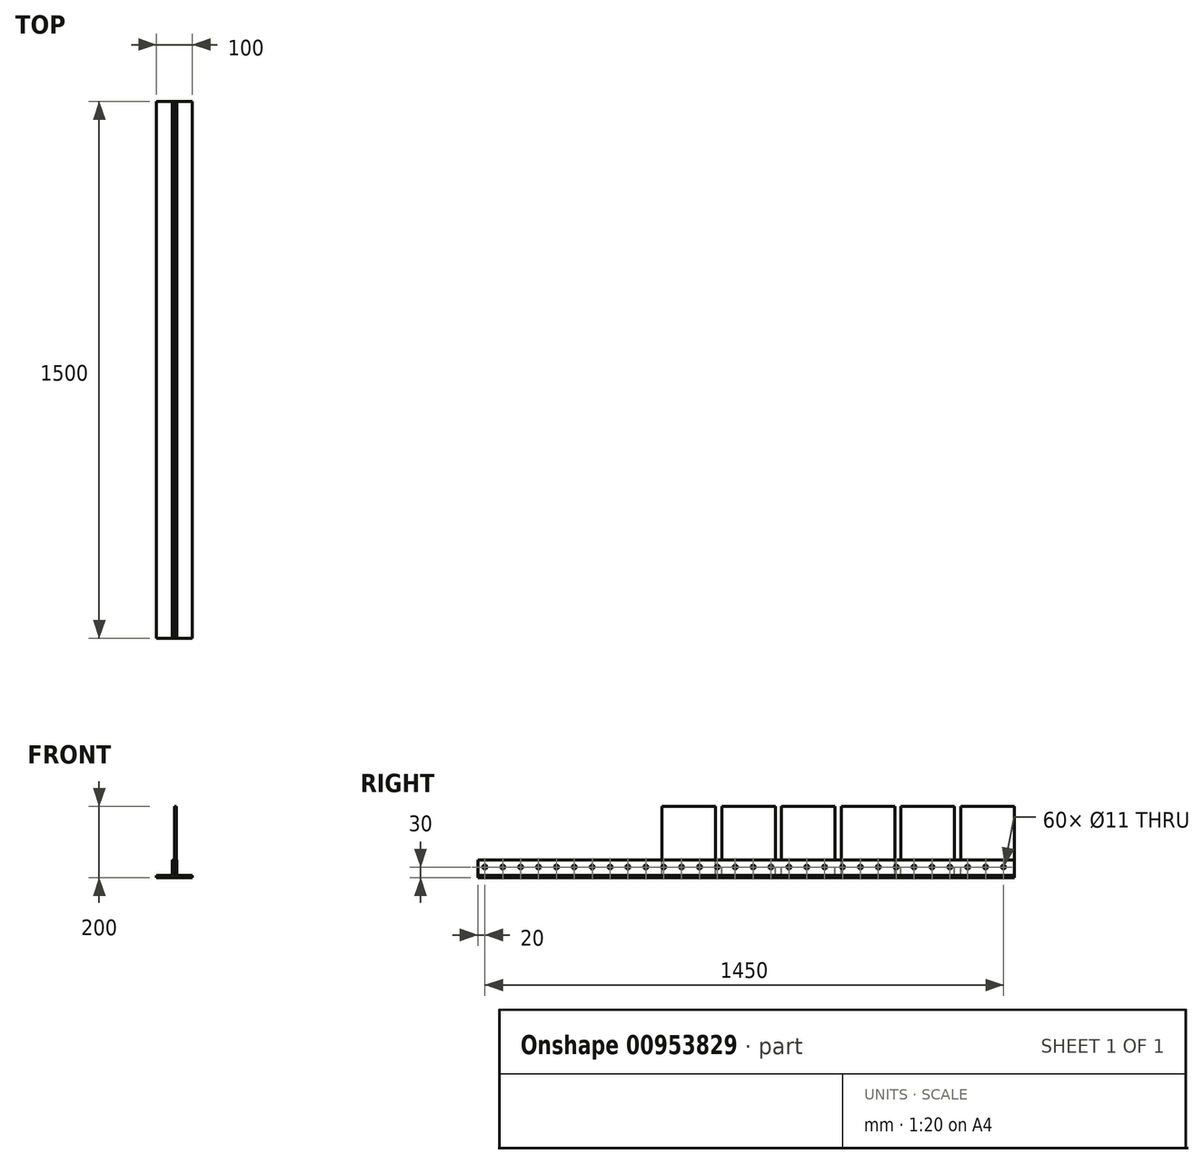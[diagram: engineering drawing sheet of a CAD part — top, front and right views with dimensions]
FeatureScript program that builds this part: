
annotation { "Feature Type Name" : "Feature", "Feature Type Description" : "" }
export const myFeature = defineFeature(function(context is Context, id is Id, definition is map)
    precondition{}
    {
        {
            var Q0;
            Q0=qCreatedBy(makeId("Front.planeOp"),FACE);
            var sketch = newSketch(context, id + "F0", { "sketchPlane" : qUnion([Q0])});
            skLineSegment(sketch, "E0", {"start": v(0, 0) * mm, "end": v(50, 0) * mm});
            skLineSegment(sketch, "E1", {"start": v(50, 0) * mm, "end": v(50, 6) * mm});
            skLineSegment(sketch, "E2", {"start": v(50, 6) * mm, "end": v(6, 6) * mm});
            skLineSegment(sketch, "E3", {"start": v(6, 6) * mm, "end": v(6, 50) * mm});
            skLineSegment(sketch, "E4", {"start": v(6, 50) * mm, "end": v(0, 50) * mm});
            skLineSegment(sketch, "E5", {"start": v(0, 50) * mm, "end": v(0, 0) * mm});
            skSolve(sketch);
        }
        {
            var Q0;
            Q0 = qSketchRegion(id + "F0", true);
            extrude(context, id + "F1", {"entities" : qUnion([Q0]), "depth" : 1500 * mm, "offsetDistance" : 25 * mm});
        }
        {
            var Q0;
            Q0=qCreatedBy(makeId("Right.planeOp"),FACE);
            var sketch = newSketch(context, id + "F2", { "sketchPlane" : qUnion([Q0])});
            skLineSegment(sketch, "E6", {"start": v(0, 0) * mm, "end": v(0, 30) * mm});
            skLineSegment(sketch, "E7", {"start": v(0, 30) * mm, "end": v(-30, 30) * mm});
            skCircle(sketch, "E8", {"center": v(-30, 30) * mm, "radius": 5.5 * mm});
            skCircle(sketch, "E9.1.0.0", {"center": v(-80, 30) * mm, "radius": 5.5 * mm});
            skCircle(sketch, "E9.2.0.0", {"center": v(-130, 30) * mm, "radius": 5.5 * mm});
            skCircle(sketch, "E9.3.0.0", {"center": v(-180, 30) * mm, "radius": 5.5 * mm});
            skCircle(sketch, "E9.4.0.0", {"center": v(-230, 30) * mm, "radius": 5.5 * mm});
            skCircle(sketch, "E9.5.0.0", {"center": v(-280, 30) * mm, "radius": 5.5 * mm});
            skCircle(sketch, "E9.6.0.0", {"center": v(-330, 30) * mm, "radius": 5.5 * mm});
            skCircle(sketch, "E9.7.0.0", {"center": v(-380, 30) * mm, "radius": 5.5 * mm});
            skCircle(sketch, "E9.8.0.0", {"center": v(-430, 30) * mm, "radius": 5.5 * mm});
            skCircle(sketch, "E9.9.0.0", {"center": v(-480, 30) * mm, "radius": 5.5 * mm});
            skCircle(sketch, "E9.10.0.0", {"center": v(-530, 30) * mm, "radius": 5.5 * mm});
            skCircle(sketch, "E9.11.0.0", {"center": v(-580, 30) * mm, "radius": 5.5 * mm});
            skCircle(sketch, "E9.12.0.0", {"center": v(-630, 30) * mm, "radius": 5.5 * mm});
            skCircle(sketch, "E9.13.0.0", {"center": v(-680, 30) * mm, "radius": 5.5 * mm});
            skCircle(sketch, "E9.14.0.0", {"center": v(-730, 30) * mm, "radius": 5.5 * mm});
            skCircle(sketch, "E9.15.0.0", {"center": v(-780, 30) * mm, "radius": 5.5 * mm});
            skCircle(sketch, "E9.16.0.0", {"center": v(-830, 30) * mm, "radius": 5.5 * mm});
            skCircle(sketch, "E9.17.0.0", {"center": v(-880, 30) * mm, "radius": 5.5 * mm});
            skCircle(sketch, "E9.18.0.0", {"center": v(-930, 30) * mm, "radius": 5.5 * mm});
            skCircle(sketch, "E9.19.0.0", {"center": v(-980, 30) * mm, "radius": 5.5 * mm});
            skCircle(sketch, "E9.20.0.0", {"center": v(-1030, 30) * mm, "radius": 5.5 * mm});
            skCircle(sketch, "E9.21.0.0", {"center": v(-1080, 30) * mm, "radius": 5.5 * mm});
            skCircle(sketch, "E9.22.0.0", {"center": v(-1130, 30) * mm, "radius": 5.5 * mm});
            skCircle(sketch, "E9.23.0.0", {"center": v(-1180, 30) * mm, "radius": 5.5 * mm});
            skCircle(sketch, "E9.24.0.0", {"center": v(-1230, 30) * mm, "radius": 5.5 * mm});
            skCircle(sketch, "E9.25.0.0", {"center": v(-1280, 30) * mm, "radius": 5.5 * mm});
            skCircle(sketch, "E9.26.0.0", {"center": v(-1330, 30) * mm, "radius": 5.5 * mm});
            skCircle(sketch, "E9.27.0.0", {"center": v(-1380, 30) * mm, "radius": 5.5 * mm});
            skCircle(sketch, "E9.28.0.0", {"center": v(-1430, 30) * mm, "radius": 5.5 * mm});
            skCircle(sketch, "E9.29.0.0", {"center": v(-1480, 30) * mm, "radius": 5.5 * mm});
            skLineSegment(sketch, "E9.direction1", {"start": v(-30, 30) * mm, "end": v(-80, 30) * mm, "construction": true});
            skSolve(sketch);
        }
        {
            var Q0;
            Q0=sQuery(id+"F2.wireOp",VERTEX,"E7.end");
            var Q1;
            Q1=sQuery(id+"F2.wireOp",VERTEX,"E9.direction1.end");
            var Q2;
            Q2=sQuery(id+"F2.wireOp",VERTEX,"E9.2.0.0.center");
            var Q3;
            Q3=sQuery(id+"F2.wireOp",VERTEX,"E9.3.0.0.center");
            var Q4;
            Q4=sQuery(id+"F2.wireOp",VERTEX,"E9.4.0.0.center");
            var Q5;
            Q5=sQuery(id+"F2.wireOp",VERTEX,"E9.5.0.0.center");
            var Q6;
            Q6=sQuery(id+"F2.wireOp",VERTEX,"E9.6.0.0.center");
            var Q7;
            Q7=sQuery(id+"F2.wireOp",VERTEX,"E9.7.0.0.center");
            var Q8;
            Q8=sQuery(id+"F2.wireOp",VERTEX,"E9.8.0.0.center");
            var Q9;
            Q9=sQuery(id+"F2.wireOp",VERTEX,"E9.9.0.0.center");
            var Q10;
            Q10=sQuery(id+"F2.wireOp",VERTEX,"E9.10.0.0.center");
            var Q11;
            Q11=sQuery(id+"F2.wireOp",VERTEX,"E9.11.0.0.center");
            var Q12;
            Q12=sQuery(id+"F2.wireOp",VERTEX,"E9.12.0.0.center");
            var Q13;
            Q13=sQuery(id+"F2.wireOp",VERTEX,"E9.13.0.0.center");
            var Q14;
            Q14=sQuery(id+"F2.wireOp",VERTEX,"E9.14.0.0.center");
            var Q15;
            Q15=sQuery(id+"F2.wireOp",VERTEX,"E9.15.0.0.center");
            var Q16;
            Q16=sQuery(id+"F2.wireOp",VERTEX,"E9.16.0.0.center");
            var Q17;
            Q17=sQuery(id+"F2.wireOp",VERTEX,"E9.17.0.0.center");
            var Q18;
            Q18=sQuery(id+"F2.wireOp",VERTEX,"E9.18.0.0.center");
            var Q19;
            Q19=sQuery(id+"F2.wireOp",VERTEX,"E9.19.0.0.center");
            var Q20;
            Q20=sQuery(id+"F2.wireOp",VERTEX,"E9.20.0.0.center");
            var Q21;
            Q21=sQuery(id+"F2.wireOp",VERTEX,"E9.21.0.0.center");
            var Q22;
            Q22=sQuery(id+"F2.wireOp",VERTEX,"E9.22.0.0.center");
            var Q23;
            Q23=sQuery(id+"F2.wireOp",VERTEX,"E9.23.0.0.center");
            var Q24;
            Q24=sQuery(id+"F2.wireOp",VERTEX,"E9.24.0.0.center");
            var Q25;
            Q25=sQuery(id+"F2.wireOp",VERTEX,"E9.25.0.0.center");
            var Q26;
            Q26=sQuery(id+"F2.wireOp",VERTEX,"E9.26.0.0.center");
            var Q27;
            Q27=sQuery(id+"F2.wireOp",VERTEX,"E9.27.0.0.center");
            var Q28;
            Q28=sQuery(id+"F2.wireOp",VERTEX,"E9.28.0.0.center");
            var Q29;
            Q29=sQuery(id+"F2.wireOp",VERTEX,"E9.29.0.0.center");
            var Q30;
            Q30=makeQuery(id+"F1.opExtrude","SWEPT_BODY",BODY,{"disambiguationData":[OSD([sQuery(id+"F0.wireOp",EDGE,"E0"),sQuery(id+"F0.wireOp",EDGE,"E1"),sQuery(id+"F0.wireOp",EDGE,"E2"),sQuery(id+"F0.wireOp",EDGE,"E3"),sQuery(id+"F0.wireOp",EDGE,"E4"),sQuery(id+"F0.wireOp",EDGE,"E5")])]});
            hole(context, id + "F3", {"style" : HoleStyle.SIMPLE, "endStyle" : HoleEndStyle.THROUGH, "oppositeDirection" : true, "holeDiameter" : 11 * mm, "majorDiameter" : 5 * mm, "isTappedThrough" : true, "tappedDepth" : 14.75 * mm, "tapClearance" : 3, "locations" : qUnion([Q0, Q1, Q2, Q3, Q4, Q5, Q6, Q7, Q8, Q9, Q10, Q11, Q12, Q13, Q14, Q15, Q16, Q17, Q18, Q19, Q20, Q21, Q22, Q23, Q24, Q25, Q26, Q27, Q28, Q29]), "scope" : qUnion([Q30])});
        }
        {
            var Q0;
            Q0=makeQuery(id+"F1.opExtrude","SWEPT_BODY",BODY,{"disambiguationData":[OSD([sQuery(id+"F0.wireOp",EDGE,"E0"),sQuery(id+"F0.wireOp",EDGE,"E1"),sQuery(id+"F0.wireOp",EDGE,"E2"),sQuery(id+"F0.wireOp",EDGE,"E3"),sQuery(id+"F0.wireOp",EDGE,"E4"),sQuery(id+"F0.wireOp",EDGE,"E5")])]});
            var Q1;
            Q1=qCreatedBy(makeId("Right.planeOp"),FACE);
            mirror(context, id + "F4", {"entities" : qUnion([Q0]), "mirrorPlane" : qUnion([Q1])});
        }
        {
            var Q0;
            Q0=qCreatedBy(makeId("Right.planeOp"),FACE);
            var sketch = newSketch(context, id + "F5", { "sketchPlane" : qUnion([Q0])});
            skLineSegment(sketch, "E10.bottom", {"start": v(0, 0) * mm, "end": v(-150, 0) * mm});
            skLineSegment(sketch, "E10.top", {"start": v(0, 200) * mm, "end": v(-150, 200) * mm});
            skLineSegment(sketch, "E10.left", {"start": v(0, 0) * mm, "end": v(0, 200) * mm});
            skLineSegment(sketch, "E10.right", {"start": v(-150, 0) * mm, "end": v(-150, 200) * mm});
            skLineSegment(sketch, "E11.1.0.0", {"start": v(-167, 0) * mm, "end": v(-167, 200) * mm});
            skLineSegment(sketch, "E11.1.0.1", {"start": v(-167, 0) * mm, "end": v(-317, 0) * mm});
            skLineSegment(sketch, "E11.1.0.2", {"start": v(-317, 0) * mm, "end": v(-317, 200) * mm});
            skLineSegment(sketch, "E11.1.0.3", {"start": v(-167, 200) * mm, "end": v(-317, 200) * mm});
            skLineSegment(sketch, "E11.2.0.0", {"start": v(-334, 0) * mm, "end": v(-334, 200) * mm});
            skLineSegment(sketch, "E11.2.0.1", {"start": v(-334, 0) * mm, "end": v(-484, 0) * mm});
            skLineSegment(sketch, "E11.2.0.2", {"start": v(-484, 0) * mm, "end": v(-484, 200) * mm});
            skLineSegment(sketch, "E11.2.0.3", {"start": v(-334, 200) * mm, "end": v(-484, 200) * mm});
            skLineSegment(sketch, "E11.3.0.0", {"start": v(-501, 0) * mm, "end": v(-501, 200) * mm});
            skLineSegment(sketch, "E11.3.0.1", {"start": v(-501, 0) * mm, "end": v(-651, 0) * mm});
            skLineSegment(sketch, "E11.3.0.2", {"start": v(-651, 0) * mm, "end": v(-651, 200) * mm});
            skLineSegment(sketch, "E11.3.0.3", {"start": v(-501, 200) * mm, "end": v(-651, 200) * mm});
            skLineSegment(sketch, "E11.4.0.0", {"start": v(-668, 0) * mm, "end": v(-668, 200) * mm});
            skLineSegment(sketch, "E11.4.0.1", {"start": v(-668, 0) * mm, "end": v(-818, 0) * mm});
            skLineSegment(sketch, "E11.4.0.2", {"start": v(-818, 0) * mm, "end": v(-818, 200) * mm});
            skLineSegment(sketch, "E11.4.0.3", {"start": v(-668, 200) * mm, "end": v(-818, 200) * mm});
            skLineSegment(sketch, "E11.5.0.0", {"start": v(-835, 0) * mm, "end": v(-835, 200) * mm});
            skLineSegment(sketch, "E11.5.0.1", {"start": v(-835, 0) * mm, "end": v(-985, 0) * mm});
            skLineSegment(sketch, "E11.5.0.2", {"start": v(-985, 0) * mm, "end": v(-985, 200) * mm});
            skLineSegment(sketch, "E11.5.0.3", {"start": v(-835, 200) * mm, "end": v(-985, 200) * mm});
            skLineSegment(sketch, "E11.direction1", {"start": v(-150, 0) * mm, "end": v(-317, 0) * mm, "construction": true});
            skSolve(sketch);
        }
        {
            var Q0;
            Q0 = qSketchRegion(id + "F5", true);
            extrude(context, id + "F6", {"entities" : qUnion([Q0]), "depth" : 5 * mm, "offsetDistance" : 25 * mm});
        }
    });
